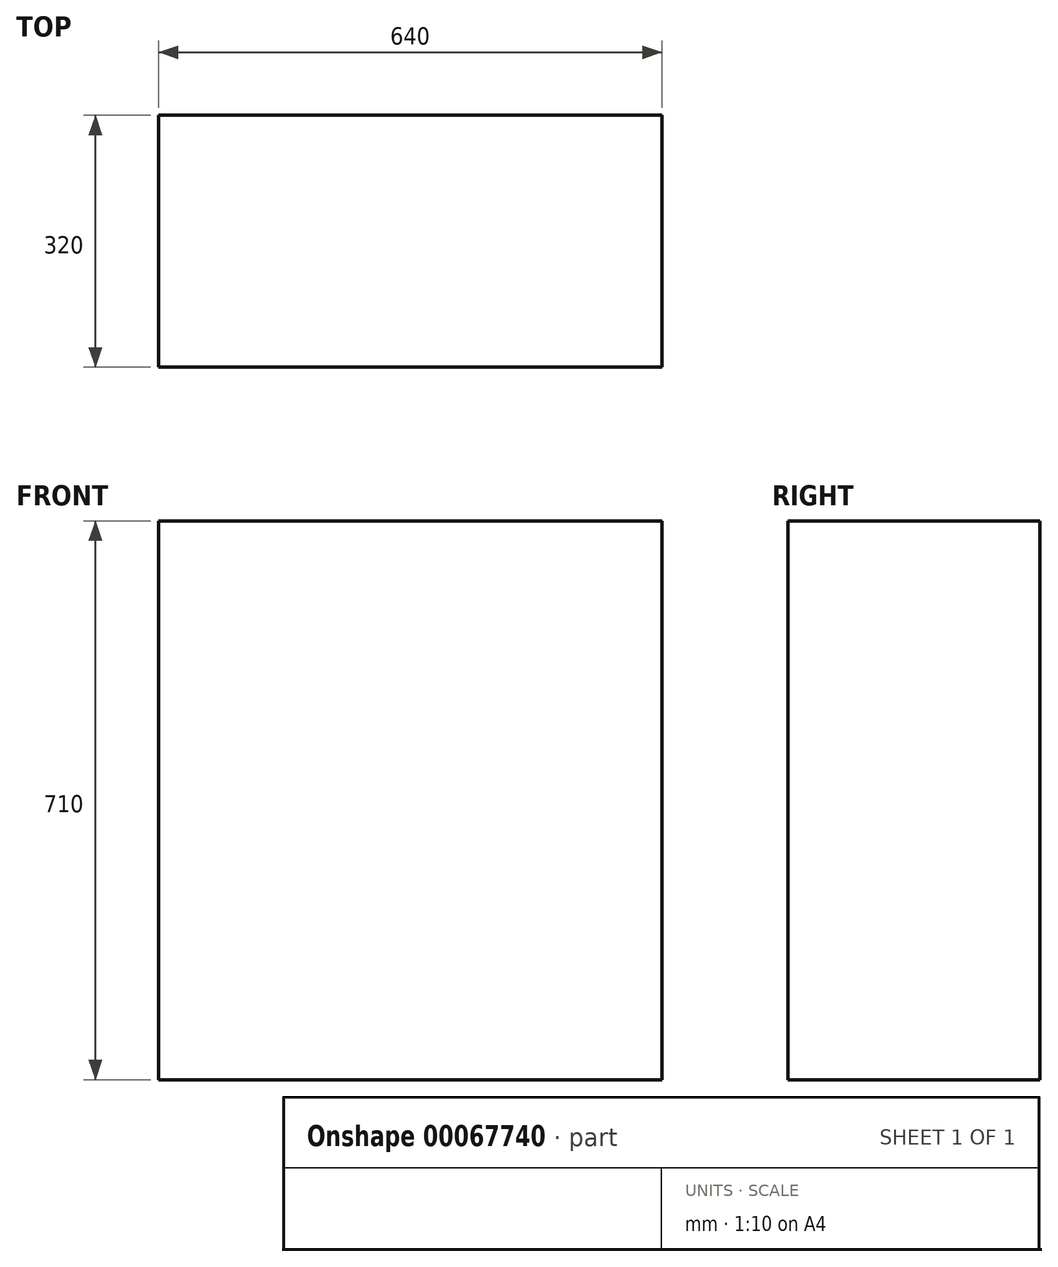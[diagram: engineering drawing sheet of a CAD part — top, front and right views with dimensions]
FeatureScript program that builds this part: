
annotation { "Feature Type Name" : "Feature", "Feature Type Description" : "" }
export const myFeature = defineFeature(function(context is Context, id is Id, definition is map)
    precondition{}
    {
        {
            var Q0;
            Q0=qCreatedBy(makeId("Front.planeOp"),FACE);
            var sketch = newSketch(context, id + "F0", { "sketchPlane" : qUnion([Q0])});
            skLineSegment(sketch, "E0", {"start": v(0, 0) * mm, "end": v(640, 0) * mm});
            skLineSegment(sketch, "E1", {"start": v(640, 0) * mm, "end": v(640, 710) * mm});
            skLineSegment(sketch, "E2", {"start": v(640, 710) * mm, "end": v(0, 710) * mm});
            skLineSegment(sketch, "E3", {"start": v(0, 710) * mm, "end": v(0, 0) * mm});
            skSolve(sketch);
        }
        {
            var Q0;
            Q0=makeQuery(id+"F0.imprint","IMPRINT",FACE,{"disambiguationData":[TD([[makeQuery(id+"F0.imprint","IMPRINT",EDGE,{"derivedFrom":sQuery(id+"F0.wireOp",EDGE,"E0")}),1.0]])]});
            extrude(context, id + "F1", {"entities" : qUnion([Q0]), "depth" : 320 * mm});
        }
    });
